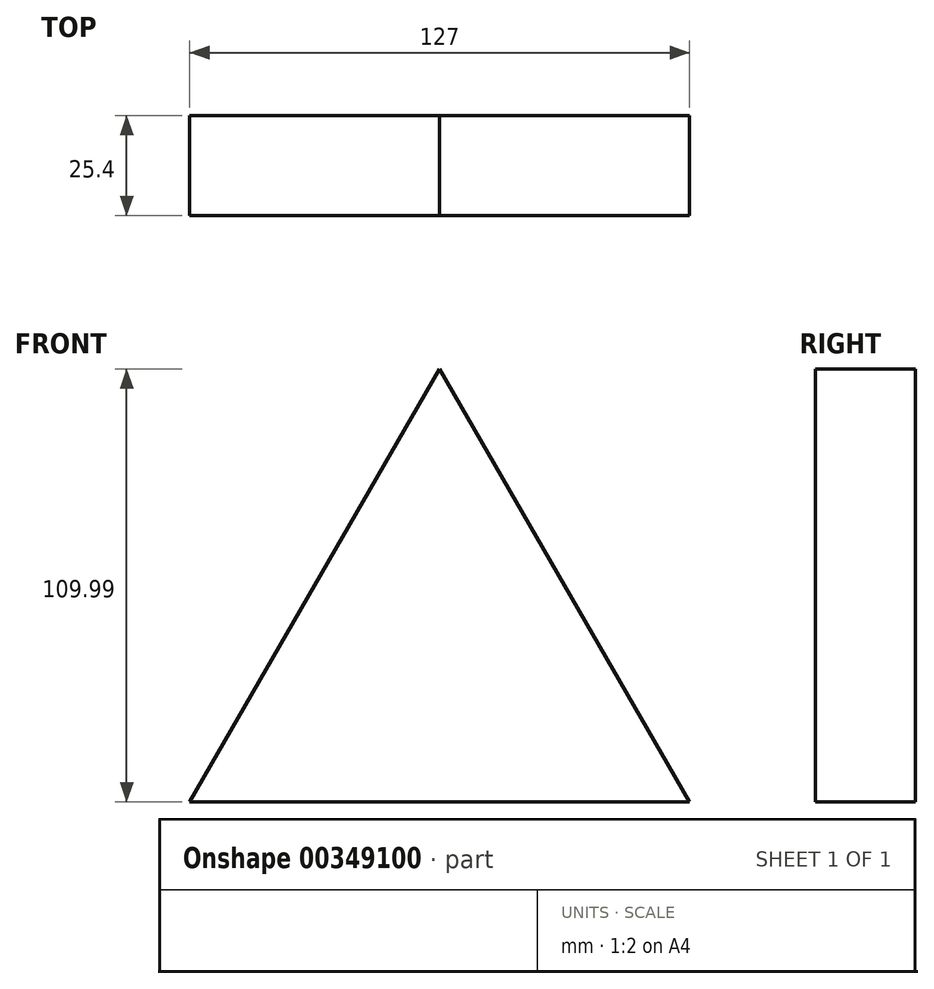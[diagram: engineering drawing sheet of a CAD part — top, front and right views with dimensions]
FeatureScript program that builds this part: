
annotation { "Feature Type Name" : "Feature", "Feature Type Description" : "" }
export const myFeature = defineFeature(function(context is Context, id is Id, definition is map)
    precondition{}
    {
        {
            var Q0;
            Q0=qCreatedBy(makeId("Front.planeOp"),FACE);
            var sketch = newSketch(context, id + "F0", { "sketchPlane" : qUnion([Q0])});
            skLineSegment(sketch, "E0", {"start": v(-63.5, 0) * mm, "end": v(63.5, 0) * mm});
            skLineSegment(sketch, "E1", {"start": v(-63.5, 0) * mm, "end": v(0, 109.99) * mm});
            skLineSegment(sketch, "E2", {"start": v(63.5, 0) * mm, "end": v(0, 109.99) * mm});
            skSolve(sketch);
        }
        {
            var Q0;
            Q0 = qSketchRegion(id + "F0", true);
            extrude(context, id + "F1", {"entities" : qUnion([Q0]), "depth" : 25.4 * mm});
        }
    });
